# Revit family: 2000_EBLOne Control Panel
name_source: partatom
category: Fire Alarm Devices
units: mm (PartAtom-declared; Revit-internal decimal feet)

## family parameters
Cut with Voids When Loaded = No
Host = Face
Maintain Annotation Orientation = No
OmniClass Number = 23.85.30.21
OmniClass Title = Environmental Detection/Registration
Part Type = Normal
Room Calculation Point = No
Round Connector Dimension = Use Diameter
Shared = No

## types (1)
- 2000
    Ambient Humidity = Maximum 95 % RH
    Ambient Temperature Operating = -5°C to +40°C
    Ambient Temperature Storage = -30°C to +60°C
    Default Elevation = 0 mm  [stored 0 ft]
    Depth (mm) = 122 mm  [stored 0.400262 ft]
    Description = Control and Indicating Equipment EBLOne.
    Height (mm) = 422 mm  [stored 1.38451 ft]
    Ingress Protection Rating = IP30
    Manufacturer = Panasonic
    Max. COM Loop Repeaters = 4
    Model = 2000
    Mounting = Wall
    Number of Loops = 1
    Omniclass Code = 23.85.30.21.11.11.11
    Omniclass Description = Smoke Detectors
    Product Material = FR ABS and polycarbonate_Panasonic_White
    Screen_Material = FR ABS and polycarbonate_Panasonic_Black
    Short Circuit Isolator = Yes, for one loop
    Tested and Approved = EN54-4, EN54-2
    Type Comments = EBLOne is a microprocessor controlled intelligent fire alarm system, intended for analog addressable detectors. EBLOne has one loop connected for addressable units. On the COM loop it is possible to connect up to four SUB-loops. Programmable control outputs and output units are available. EBLOne consists of a colour touch screen and has multi language support. EBLOne can have up to 253 addresses and up to 253 alarm points.
    URL = https://www.panasonic-fire-security.com
    Uniclass 2015 Code = Pr_75_80_30_27
    Uniclass 2015 Description = Fire and smoke detector bases
    Uniformat 2010  Code = D7050
    Uniformat 2010 Description = Detection and Alarm
    Version = RVT20
    Voltage Primary = 230VAC (195 - 253) 1.1A, 50Hz
    Voltage System = 24 VDC
    Weight = 4000 g
    Width (mm) = 310 mm  [stored 1.01706 ft]

note: [stored X ft] marks values corroborated as IEEE doubles in the binary element streams (Revit-internal decimal feet)

## geometry (parser evidence)
native form markers: Blend x87, Sweep x2
no freeform markers — native parametric forms only
